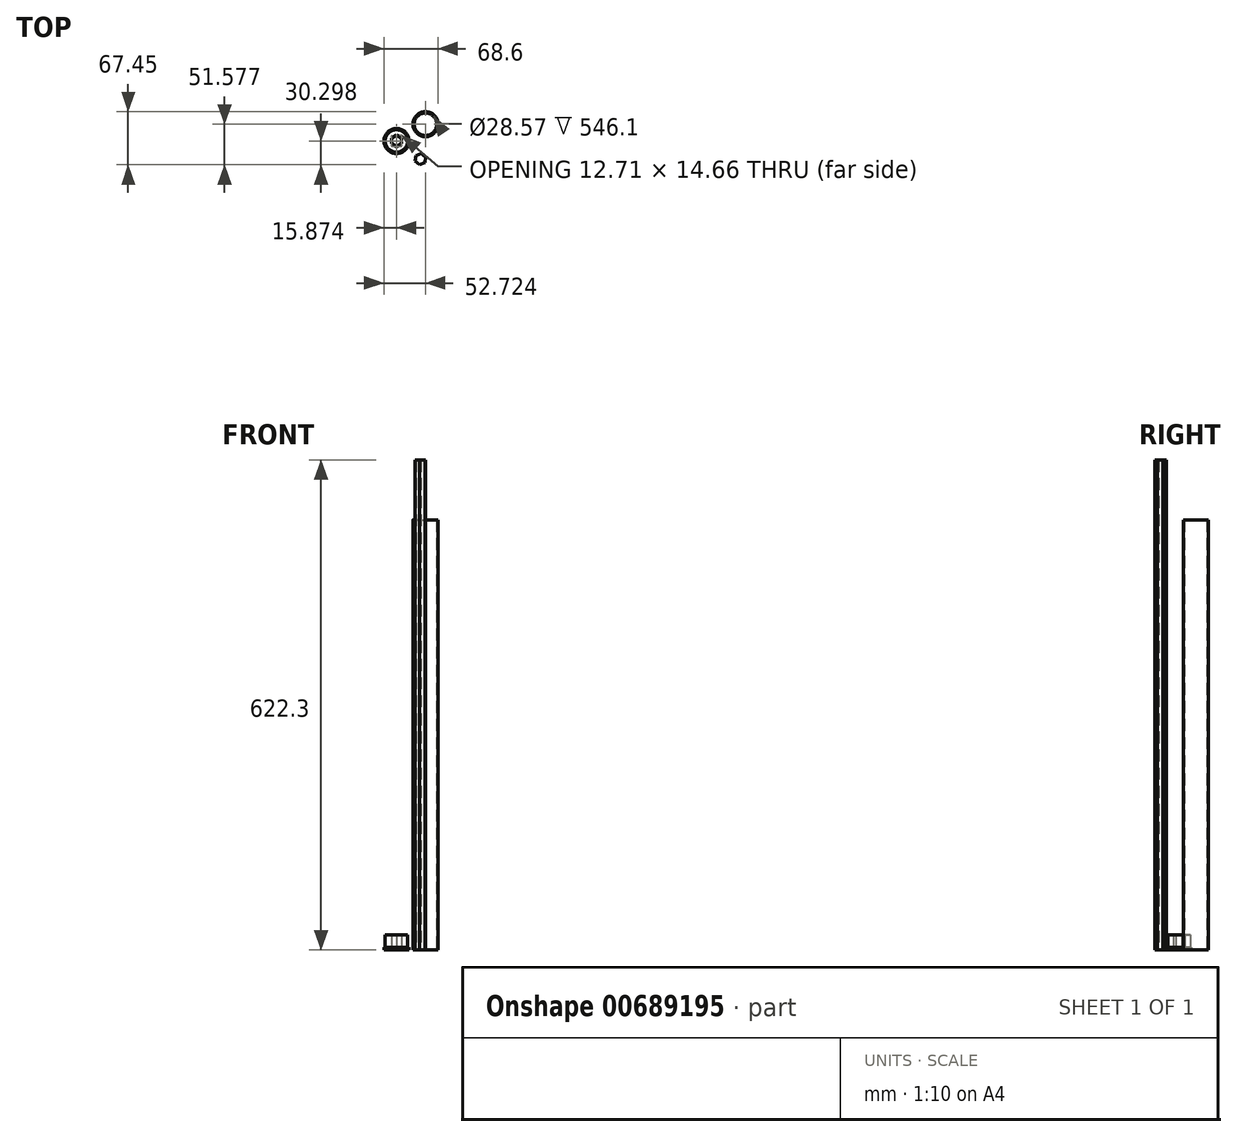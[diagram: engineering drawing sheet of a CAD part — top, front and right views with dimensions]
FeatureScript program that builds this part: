
annotation { "Feature Type Name" : "Feature", "Feature Type Description" : "" }
export const myFeature = defineFeature(function(context is Context, id is Id, definition is map)
    precondition{}
    {
        {
            assignVariable(context, id + "F0", {"name" : "drum_length", "anyValue" : 546.1 * mm});
        }
        {
            var Q0;
            Q0=qCreatedBy(makeId("Top.planeOp"),FACE);
            var sketch = newSketch(context, id + "F1", { "sketchPlane" : qUnion([Q0])});
            skCircle(sketch, "E0", {"center": v(-50.46, 45.65) * mm, "radius": 15.88 * mm});
            skCircle(sketch, "E1", {"center": v(-50.46, 45.65) * mm, "radius": 14.29 * mm});
            skCircle(sketch, "E2.cCircle", {"center": v(-50.46, 45.65) * mm, "radius": 6.35 * mm, "construction": true});
            skLineSegment(sketch, "E2.0", {"start": v(-56.8, 49.32) * mm, "end": v(-50.45, 52.98) * mm});
            skLineSegment(sketch, "E2.1", {"start": v(-50.45, 52.98) * mm, "end": v(-44.1, 49.3) * mm});
            skLineSegment(sketch, "E2.2", {"start": v(-44.1, 49.3) * mm, "end": v(-44.11, 41.97) * mm});
            skLineSegment(sketch, "E2.3", {"start": v(-44.11, 41.97) * mm, "end": v(-50.46, 38.32) * mm});
            skLineSegment(sketch, "E2.4", {"start": v(-50.46, 38.32) * mm, "end": v(-56.81, 41.99) * mm});
            skLineSegment(sketch, "E2.5", {"start": v(-56.81, 41.99) * mm, "end": v(-56.8, 49.32) * mm});
            skPoint(sketch, "E2.0.midPoint", {"position": v(-53.62, 51.15) * mm});
            skSolve(sketch);
        }
        {
            var Q0;
            Q0=makeQuery(id+"F1.imprint","IMPRINT",FACE,{"disambiguationData":[TD([[makeQuery(id+"F1.imprint","IMPRINT",EDGE,{"derivedFrom":sQuery(id+"F1.wireOp",EDGE,"E0")}),1.0]])]});
            extrude(context, id + "F2", {"entities" : qUnion([Q0]), "depth" : 3.17 * mm, "offsetDistance" : 25.4 * mm});
        }
        {
            var Q0;
            Q0=makeQuery(id+"F1.imprint","IMPRINT",FACE,{"disambiguationData":[TD([[makeQuery(id+"F1.imprint","IMPRINT",EDGE,{"derivedFrom":sQuery(id+"F1.wireOp",EDGE,"E1")}),1.0]])]});
            extrude(context, id + "F3", {"entities" : qUnion([Q0]), "operationType" : NewBodyOperationType.ADD, "depth" : 19.05 * mm, "offsetDistance" : 25.4 * mm});
        }
        {
            var Q0;
            Q0=qCreatedBy(makeId("Top.planeOp"),FACE);
            var sketch = newSketch(context, id + "F4", { "sketchPlane" : qUnion([Q0])});
            skCircle(sketch, "E3", {"center": v(-13.6, 66.93) * mm, "radius": 14.29 * mm});
            skCircle(sketch, "E4", {"center": v(-13.6, 66.93) * mm, "radius": 15.88 * mm});
            skSolve(sketch);
        }
        {
            var Q0;
            Q0=makeQuery(id+"F4.imprint","IMPRINT",FACE,{"disambiguationData":[TD([[makeQuery(id+"F4.imprint","IMPRINT",EDGE,{"derivedFrom":sQuery(id+"F4.wireOp",EDGE,"E3")}),-1.0]])]});
            extrude(context, id + "F5", {"entities" : qUnion([Q0]), "depth" : getVariable(context, 'drum_length'), "offsetDistance" : 25.4 * mm});
        }
        {
            var Q0;
            Q0=qCreatedBy(makeId("Top.planeOp"),FACE);
            var sketch = newSketch(context, id + "F6", { "sketchPlane" : qUnion([Q0])});
            skCircle(sketch, "E5.cCircle", {"center": v(-20.07, 22.6) * mm, "radius": 6.35 * mm, "construction": true});
            skLineSegment(sketch, "E5.0", {"start": v(-14.34, 18.02) * mm, "end": v(-21.17, 15.35) * mm});
            skLineSegment(sketch, "E5.1", {"start": v(-21.17, 15.35) * mm, "end": v(-26.9, 19.92) * mm});
            skLineSegment(sketch, "E5.2", {"start": v(-26.9, 19.92) * mm, "end": v(-25.8, 27.17) * mm});
            skLineSegment(sketch, "E5.3", {"start": v(-25.8, 27.17) * mm, "end": v(-18.97, 29.84) * mm});
            skLineSegment(sketch, "E5.4", {"start": v(-18.97, 29.84) * mm, "end": v(-13.24, 25.27) * mm});
            skLineSegment(sketch, "E5.5", {"start": v(-13.24, 25.27) * mm, "end": v(-14.34, 18.02) * mm});
            skPoint(sketch, "E5.0.midPoint", {"position": v(-17.76, 16.68) * mm});
            skSolve(sketch);
        }
        {
            var Q0;
            Q0=makeQuery(id+"F6.imprint","IMPRINT",FACE,{"disambiguationData":[TD([[makeQuery(id+"F6.imprint","IMPRINT",EDGE,{"derivedFrom":sQuery(id+"F6.wireOp",EDGE,"E5.0")}),-1.0]])]});
            extrude(context, id + "F7", {"entities" : qUnion([Q0]), "depth" : getVariable(context, 'drum_length') + 76.2 * mm, "offsetDistance" : 25.4 * mm});
        }
    });
